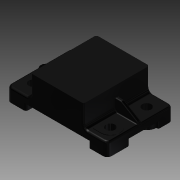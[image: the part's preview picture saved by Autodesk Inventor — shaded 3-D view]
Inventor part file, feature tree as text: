
AUTODESK INVENTOR PART (.ipt)
format: ipt  version: 2014 SP1 (Build 180222100, 222)  size: 528,896 bytes
history: native  units: mm (DEFAULTED — no unit token found)
features: sketch x12, extrude x11, fillet x5, plane x4, mirror x3, rib x1
ambient origin geometry x8: Origin, YZ Plane, XZ Plane, XY Plane, X Axis, Y Axis, Z Axis, Center Point
bodies: Solid1 (feature_tree)
feature tree (36):
  extrude  "Extrusion1"  Depth=5.08mm
  fillet  "Fillet19"  Radius=73.66mm
  plane  "Work Plane6"
  plane  "Work Plane7"
  extrude  "Extrusion4"  Depth=48.26mm TaperAngle=0.0deg
  fillet  "Fillet20"  Radius=3.048mm
  extrude  "Extrusion10"  Depth=1.524mm
  extrude  "Extrusion12"  Depth=8.89mm TaperAngle=0.0deg
  fillet  "Fillet21"  Radius=0.381mm
  plane  "Work Plane3"
  plane  "Work Plane4"
  mirror  "Mirror4"
  mirror  "Mirror5"
  extrude  "Extrusion11"  Depth=3.302mm
  extrude  "Extrusion13"  Depth=8.636mm
  extrude  "Extrusion14"  Depth=2.54mm
  extrude  "Extrusion15"  Depth=0.762mm
  extrude  "Extrusion16"  Depth=3.048mm
  extrude  "Extrusion5"  Depth=13.97mm
  extrude  "Extrusion6"  Depth=4.826mm TaperAngle=0.0deg
  rib  "Rib2"
  fillet  "Fillet22"  Radius=1.27mm
  fillet  "Fillet23"  Radius=4.826mm
  mirror  "Mirror6"
  sketch  "Sketch1"  dims[d1=21.336mm d2=5.08mm d3=73.66mm]
  sketch  "Sketch5"  dims[d4=38.862mm d5=48.26mm d6=0.0mm d40=3.048mm]
  sketch  "Sketch6"  dims[d41=3.048mm d42=1.524mm]
  sketch  "Sketch7"  dims[d43=6.604mm d46=8.89mm d47=0.0mm d48=0.381mm d49=0.0mm]
  sketch  "Sketch8"  dims[d50=0.381mm d51=0.0mm d52=3.302mm]
  sketch  "Sketch14"  dims[d53=3.302mm d54=8.636mm]
  sketch  "Sketch15"  dims[d55=3.302mm d56=2.54mm]
  sketch  "Sketch16"  dims[d57=2.54mm d58=0.762mm]
  sketch  "Sketch17"  dims[d59=0.762mm d83=3.048mm]
  sketch  "Sketch18"  dims[d84=1.524mm d85=13.97mm]
  sketch  "Sketch19"  dims[d86=16.51mm d87=4.826mm d88=0.0mm d89=1.27mm d90=4.826mm d91=0.0mm]
  sketch  "Sketch20"  dims[d92=3.048mm d93=1.524mm d94=16.51mm d95=13.97mm d96=4.826mm d97=0.0mm d98=1.27mm d99=4.826mm d100=0.0mm d101=13.97mm d102=13.97mm d103=3.048mm d104=1.524mm d105=1.016mm d106=3.048mm d107=1.524mm d108=1.016mm d109=13.97mm d110=4.826mm d111=0.0mm d112=1.27mm d113=1.27mm d114=0.381mm d116=0.381mm d117=13.97mm d118=4.826mm d119=0.0mm d120=1.27mm d121=0.381mm d122=0.381mm d124=13.97mm d125=4.826mm d126=0.0mm d127=13.335mm d128=28.321mm]
